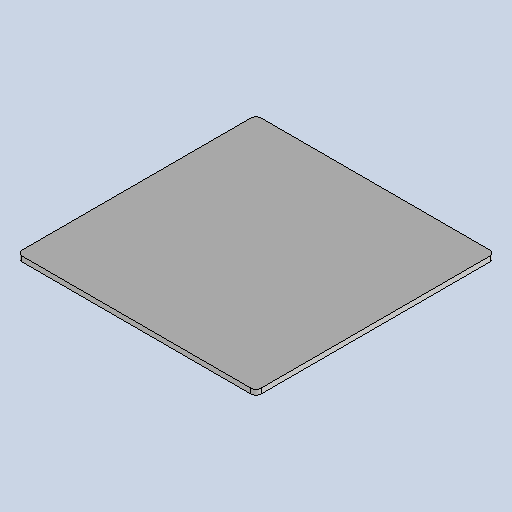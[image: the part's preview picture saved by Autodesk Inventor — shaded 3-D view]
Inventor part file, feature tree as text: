
AUTODESK INVENTOR PART (.ipt)
format: ipt  version: 2025.1 (Build 291241020, 241B)  size: 139,264 bytes
history: native  units: mm
features: other x2, sheet_metal_op x1, chamfer x1, sketch x1
ambient origin geometry x8: Origin, YZ Plane, XZ Plane, XY Plane, X Axis, Y Axis, Z Axis, Center Point
bodies: Body1 (feature_tree)
feature tree (5):
  sheet_metal_op  "Face3"
  chamfer  "Corner Round1"
  sketch  "Sketch1"  dims[d154=94.0mm d155=94.0mm d156=2.0mm d178=2.0mm]
  other  "Plate5"
  other  "Definition1"
